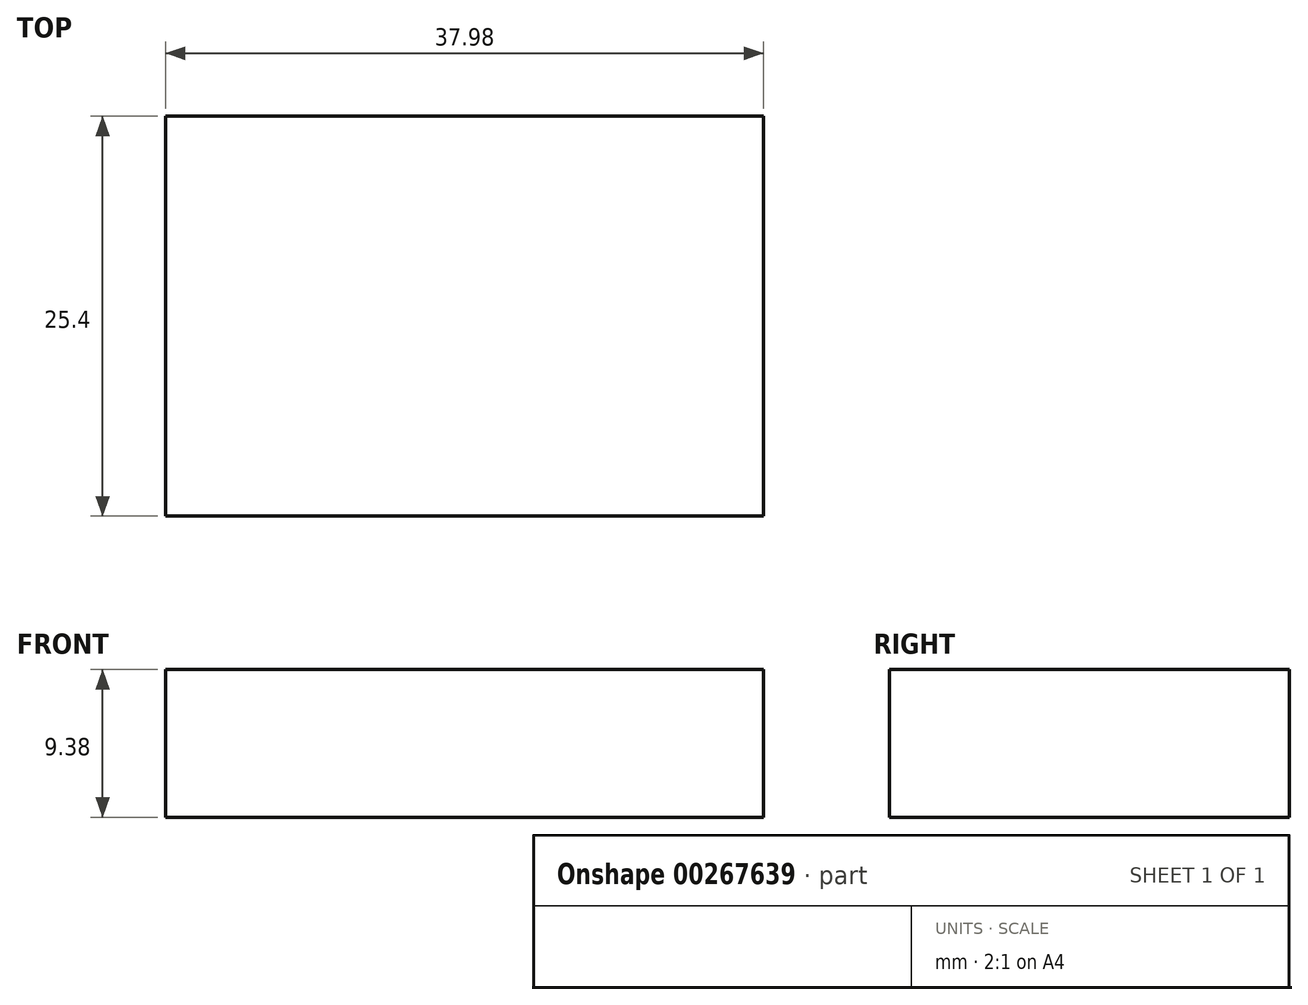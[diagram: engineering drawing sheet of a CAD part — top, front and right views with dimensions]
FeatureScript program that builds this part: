
annotation { "Feature Type Name" : "Feature", "Feature Type Description" : "" }
export const myFeature = defineFeature(function(context is Context, id is Id, definition is map)
    precondition{}
    {
        {
            var Q0;
            Q0=qCreatedBy(makeId("Front.planeOp"),FACE);
            var sketch = newSketch(context, id + "F0", { "sketchPlane" : qUnion([Q0])});
            skLineSegment(sketch, "E0.bottom", {"start": v(18.99, 4.7) * mm, "end": v(-18.99, 4.7) * mm});
            skLineSegment(sketch, "E0.top", {"start": v(18.99, -4.7) * mm, "end": v(-18.99, -4.7) * mm});
            skLineSegment(sketch, "E0.left", {"start": v(18.99, 4.7) * mm, "end": v(18.99, -4.7) * mm});
            skLineSegment(sketch, "E0.right", {"start": v(-18.99, 4.7) * mm, "end": v(-18.99, -4.7) * mm});
            skPoint(sketch, "E0.middle", {"position": v(0, 0) * mm});
            skSolve(sketch);
        }
        {
            var Q0;
            Q0=makeQuery(id+"F0.imprint","IMPRINT",FACE,{"disambiguationData":[TD([[makeQuery(id+"F0.imprint","IMPRINT",EDGE,{"derivedFrom":sQuery(id+"F0.wireOp",EDGE,"E0.bottom")}),1.0]])]});
            extrude(context, id + "F1", {"entities" : qUnion([Q0]), "oppositeDirection" : true, "depth" : 25.4 * mm});
        }
    });
